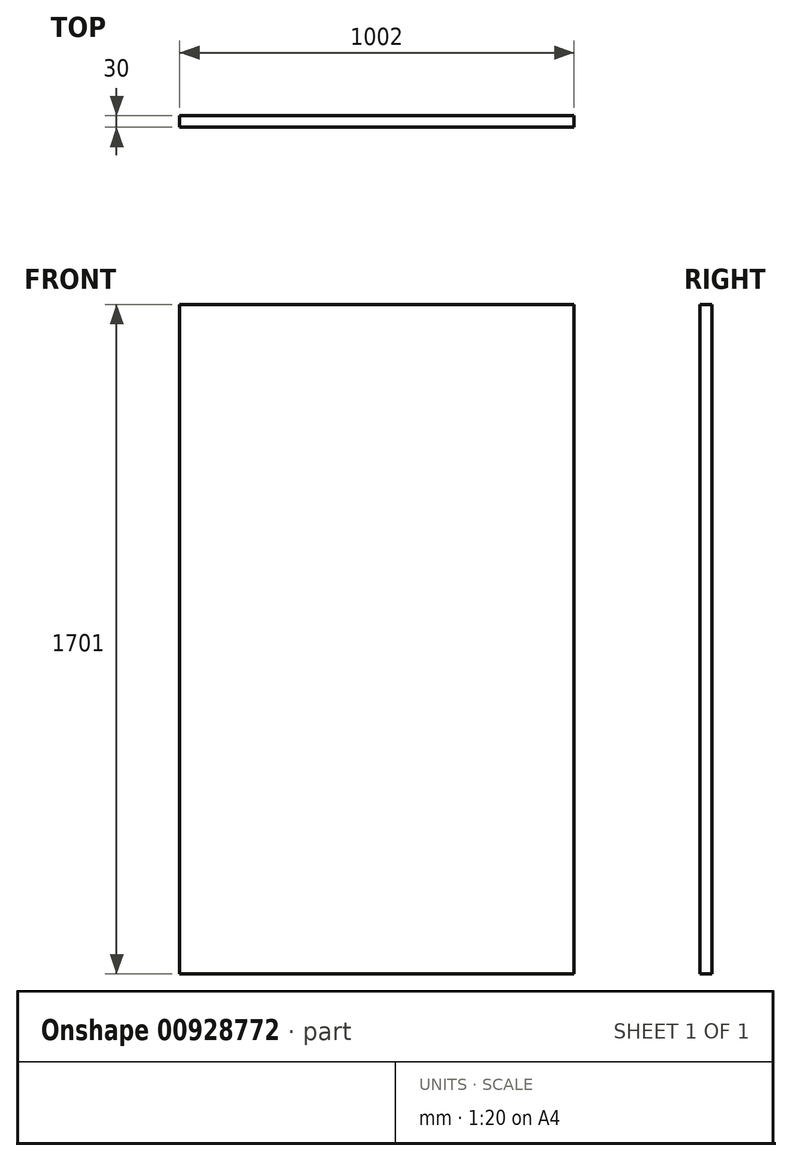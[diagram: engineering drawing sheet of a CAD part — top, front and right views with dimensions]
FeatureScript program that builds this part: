
annotation { "Feature Type Name" : "Feature", "Feature Type Description" : "" }
export const myFeature = defineFeature(function(context is Context, id is Id, definition is map)
    precondition{}
    {
        {
            var Q0;
            Q0=qCreatedBy(makeId("Front.planeOp"),FACE);
            var sketch = newSketch(context, id + "F0", { "sketchPlane" : qUnion([Q0])});
            skLineSegment(sketch, "E0.bottom", {"start": v(0, 0) * mm, "end": v(1002, 0) * mm});
            skLineSegment(sketch, "E0.top", {"start": v(0, 1701) * mm, "end": v(1002, 1701) * mm});
            skLineSegment(sketch, "E0.left", {"start": v(0, 0) * mm, "end": v(0, 1701) * mm});
            skLineSegment(sketch, "E0.right", {"start": v(1002, 0) * mm, "end": v(1002, 1701) * mm});
            skSolve(sketch);
        }
        {
            var Q0;
            Q0 = qSketchRegion(id + "F0", true);
            extrude(context, id + "F1", {"entities" : qUnion([Q0]), "depth" : 30 * mm, "offsetDistance" : 25 * mm});
        }
    });
